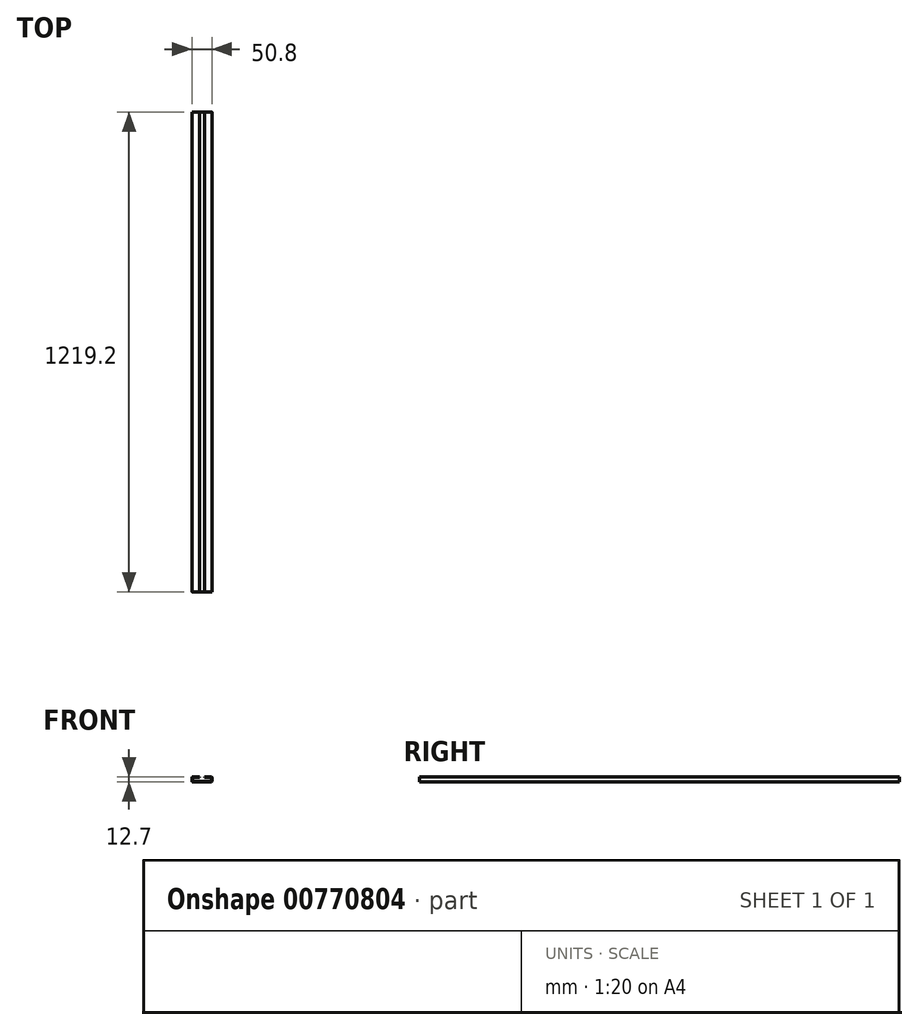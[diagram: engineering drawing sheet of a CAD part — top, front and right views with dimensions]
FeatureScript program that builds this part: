
annotation { "Feature Type Name" : "Feature", "Feature Type Description" : "" }
export const myFeature = defineFeature(function(context is Context, id is Id, definition is map)
    precondition{}
    {
        {
            var Q0;
            Q0=qCreatedBy(makeId("Front.planeOp"),FACE);
            var sketch = newSketch(context, id + "F0", { "sketchPlane" : qUnion([Q0])});
            skLineSegment(sketch, "E0", {"start": v(0, 0) * mm, "end": v(-25.4, 0) * mm});
            skLineSegment(sketch, "E1", {"start": v(-25.4, 0) * mm, "end": v(-25.4, 12.7) * mm});
            skLineSegment(sketch, "E2", {"start": v(-25.4, 12.7) * mm, "end": v(-6.35, 12.7) * mm});
            skLineSegment(sketch, "E3.0", {"start": v(-23.81, 11.11) * mm, "end": v(-6.35, 11.11) * mm});
            skLineSegment(sketch, "E3.3", {"start": v(0, 1.59) * mm, "end": v(-23.81, 1.59) * mm});
            skLineSegment(sketch, "E3.4", {"start": v(-23.81, 1.59) * mm, "end": v(-23.81, 11.11) * mm});
            skLineSegment(sketch, "E4", {"start": v(-6.35, 12.7) * mm, "end": v(-6.35, 11.11) * mm});
            skLineSegment(sketch, "E5.MirrorCS", {"start": v(6.35, 12.7) * mm, "end": v(6.35, 11.11) * mm});
            skLineSegment(sketch, "E6.MirrorCS", {"start": v(23.81, 1.59) * mm, "end": v(23.81, 11.11) * mm});
            skLineSegment(sketch, "E7.MirrorCS", {"start": v(25.4, 12.7) * mm, "end": v(6.35, 12.7) * mm});
            skLineSegment(sketch, "E8.MirrorCS", {"start": v(25.4, 0) * mm, "end": v(25.4, 12.7) * mm});
            skLineSegment(sketch, "E9.MirrorCS", {"start": v(0, 0) * mm, "end": v(25.4, 0) * mm});
            skLineSegment(sketch, "E10.MirrorCS", {"start": v(0, 1.59) * mm, "end": v(23.81, 1.59) * mm});
            skLineSegment(sketch, "E11.MirrorCS", {"start": v(23.81, 11.11) * mm, "end": v(6.35, 11.11) * mm});
            skSolve(sketch);
        }
        {
            var Q0;
            Q0=makeQuery(id+"F0.imprint","IMPRINT",FACE,{"disambiguationData":[TD([[makeQuery(id+"F0.imprint","IMPRINT",EDGE,{"derivedFrom":sQuery(id+"F0.wireOp",EDGE,"E0")}),-1.0]])]});
            extrude(context, id + "F1", {"entities" : qUnion([Q0]), "depth" : 1219.2 * mm, "offsetDistance" : 25.4 * mm});
        }
        {
            var Q0;
            Q0=makeQuery(id+"F1.opExtrude","SWEPT_EDGE",EDGE,{"disambiguationData":[OSD([sQuery(id+"F0.wireOp",EDGE,"E3.2"),sQuery(id+"F0.wireOp",EDGE,"E3.3")])]});
            var Q1;
            Q1=makeQuery(id+"F1.opExtrude","SWEPT_EDGE",EDGE,{"disambiguationData":[OSD([sQuery(id+"F0.wireOp",EDGE,"E3.3"),sQuery(id+"F0.wireOp",EDGE,"E3.4")])]});
            var Q2;
            Q2=makeQuery(id+"F1.opExtrude","SWEPT_EDGE",EDGE,{"disambiguationData":[OSD([sQuery(id+"F0.wireOp",EDGE,"E3.1"),sQuery(id+"F0.wireOp",EDGE,"E3.2")])]});
            var Q3;
            Q3=makeQuery(id+"F1.opExtrude","SWEPT_EDGE",EDGE,{"disambiguationData":[OSD([sQuery(id+"F0.wireOp",EDGE,"E3.0"),sQuery(id+"F0.wireOp",EDGE,"E3.4")])]});
            var Q4;
            Q4=makeQuery(id+"F1.opExtrude","SWEPT_EDGE",EDGE,{"disambiguationData":[OSD([sQuery(id+"F0.wireOp",EDGE,"b99351de-defc-40e2-8460-c5c30a8e78234.MirrorCS"),sQuery(id+"F0.wireOp",EDGE,"b99351de-defc-40e2-8460-c5c30a8e78239.MirrorCS")])]});
            var Q5;
            Q5=makeQuery(id+"F1.opExtrude","SWEPT_EDGE",EDGE,{"disambiguationData":[OSD([sQuery(id+"F0.wireOp",EDGE,"b99351de-defc-40e2-8460-c5c30a8e78234.MirrorCS"),sQuery(id+"F0.wireOp",EDGE,"E10.MirrorCS")])]});
            var Q6;
            Q6=makeQuery(id+"F1.opExtrude","SWEPT_EDGE",EDGE,{"disambiguationData":[OSD([sQuery(id+"F0.wireOp",EDGE,"E6.MirrorCS"),sQuery(id+"F0.wireOp",EDGE,"E10.MirrorCS")])]});
            var Q7;
            Q7=makeQuery(id+"F1.opExtrude","SWEPT_EDGE",EDGE,{"disambiguationData":[OSD([sQuery(id+"F0.wireOp",EDGE,"E6.MirrorCS"),sQuery(id+"F0.wireOp",EDGE,"E11.MirrorCS")])]});
            fillet(context, id + "F2", {"entities" : qUnion([Q0, Q1, Q2, Q3, Q4, Q5, Q6, Q7]), "radius" : 0.8 * mm, "tangentPropagation" : true, "allowEdgeOverflow" : false});
        }
        {
            var Q0;
            Q0=makeQuery(id+"F1.opExtrude","SWEPT_EDGE",EDGE,{"disambiguationData":[OSD([sQuery(id+"F0.wireOp",EDGE,"E7.MirrorCS"),sQuery(id+"F0.wireOp",EDGE,"E8.MirrorCS")])]});
            var Q1;
            Q1=makeQuery(id+"F1.opExtrude","SWEPT_EDGE",EDGE,{"disambiguationData":[OSD([sQuery(id+"F0.wireOp",EDGE,"E8.MirrorCS"),sQuery(id+"F0.wireOp",EDGE,"E9.MirrorCS")])]});
            var Q2;
            Q2=makeQuery(id+"F1.opExtrude","SWEPT_EDGE",EDGE,{"disambiguationData":[OSD([sQuery(id+"F0.wireOp",EDGE,"b99351de-defc-40e2-8460-c5c30a8e78235.MirrorCS"),sQuery(id+"F0.wireOp",EDGE,"E9.MirrorCS")])]});
            var Q3;
            Q3=makeQuery(id+"F1.opExtrude","SWEPT_EDGE",EDGE,{"disambiguationData":[OSD([sQuery(id+"F0.wireOp",EDGE,"b99351de-defc-40e2-8460-c5c30a8e78235.MirrorCS"),sQuery(id+"F0.wireOp",EDGE,"b99351de-defc-40e2-8460-c5c30a8e78238.MirrorCS")])]});
            var Q4;
            Q4=makeQuery(id+"F1.opExtrude","SWEPT_EDGE",EDGE,{"disambiguationData":[OSD([sQuery(id+"F0.wireOp",EDGE,"VWfdgoNW-Hj4l-MGz8-AwcO-IJpsfwk1iBpo"),sQuery(id+"F0.wireOp",EDGE,"cBkWsrEC-scCM-FOG8-YLiR-dLnhiUL93ZZf")])]});
            var Q5;
            Q5=makeQuery(id+"F1.opExtrude","SWEPT_EDGE",EDGE,{"disambiguationData":[OSD([sQuery(id+"F0.wireOp",EDGE,"cBkWsrEC-scCM-FOG8-YLiR-dLnhiUL93ZZf"),sQuery(id+"F0.wireOp",EDGE,"E0")])]});
            var Q6;
            Q6=makeQuery(id+"F1.opExtrude","SWEPT_EDGE",EDGE,{"disambiguationData":[OSD([sQuery(id+"F0.wireOp",EDGE,"E0"),sQuery(id+"F0.wireOp",EDGE,"E1")])]});
            var Q7;
            Q7=makeQuery(id+"F1.opExtrude","SWEPT_EDGE",EDGE,{"disambiguationData":[OSD([sQuery(id+"F0.wireOp",EDGE,"E1"),sQuery(id+"F0.wireOp",EDGE,"E2")])]});
            fillet(context, id + "F3", {"entities" : qUnion([Q0, Q1, Q2, Q3, Q4, Q5, Q6, Q7]), "radius" : 1.59 * mm, "tangentPropagation" : true, "allowEdgeOverflow" : false});
        }
    });
